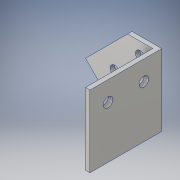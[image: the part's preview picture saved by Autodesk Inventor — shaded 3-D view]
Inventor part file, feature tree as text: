
AUTODESK INVENTOR PART (.ipt)
format: ipt  version: 2016 (Build 200138000, 138)  size: 111,104 bytes
history: native  units: in
note: dims shown in document units (in); Inventor stores cm internally (conversion verified against a paired STEP export)
features: sketch x4, other x3
ambient origin geometry x8: Origin, YZ Plane, XZ Plane, XY Plane, X Axis, Y Axis, Z Axis, Center Point
bodies: Solid1 (feature_tree)
feature tree (7):
  other  "bottom left rail gusset.ipt"
  other  "Solid1::bottom left rail gusset.ipt"
  other  "TaggingFeature1"
  sketch  "Sketch1"  dims[d0=0.3937in]
  sketch  "Sketch2"
  sketch  "Sketch3"
  sketch  "Sketch4"
